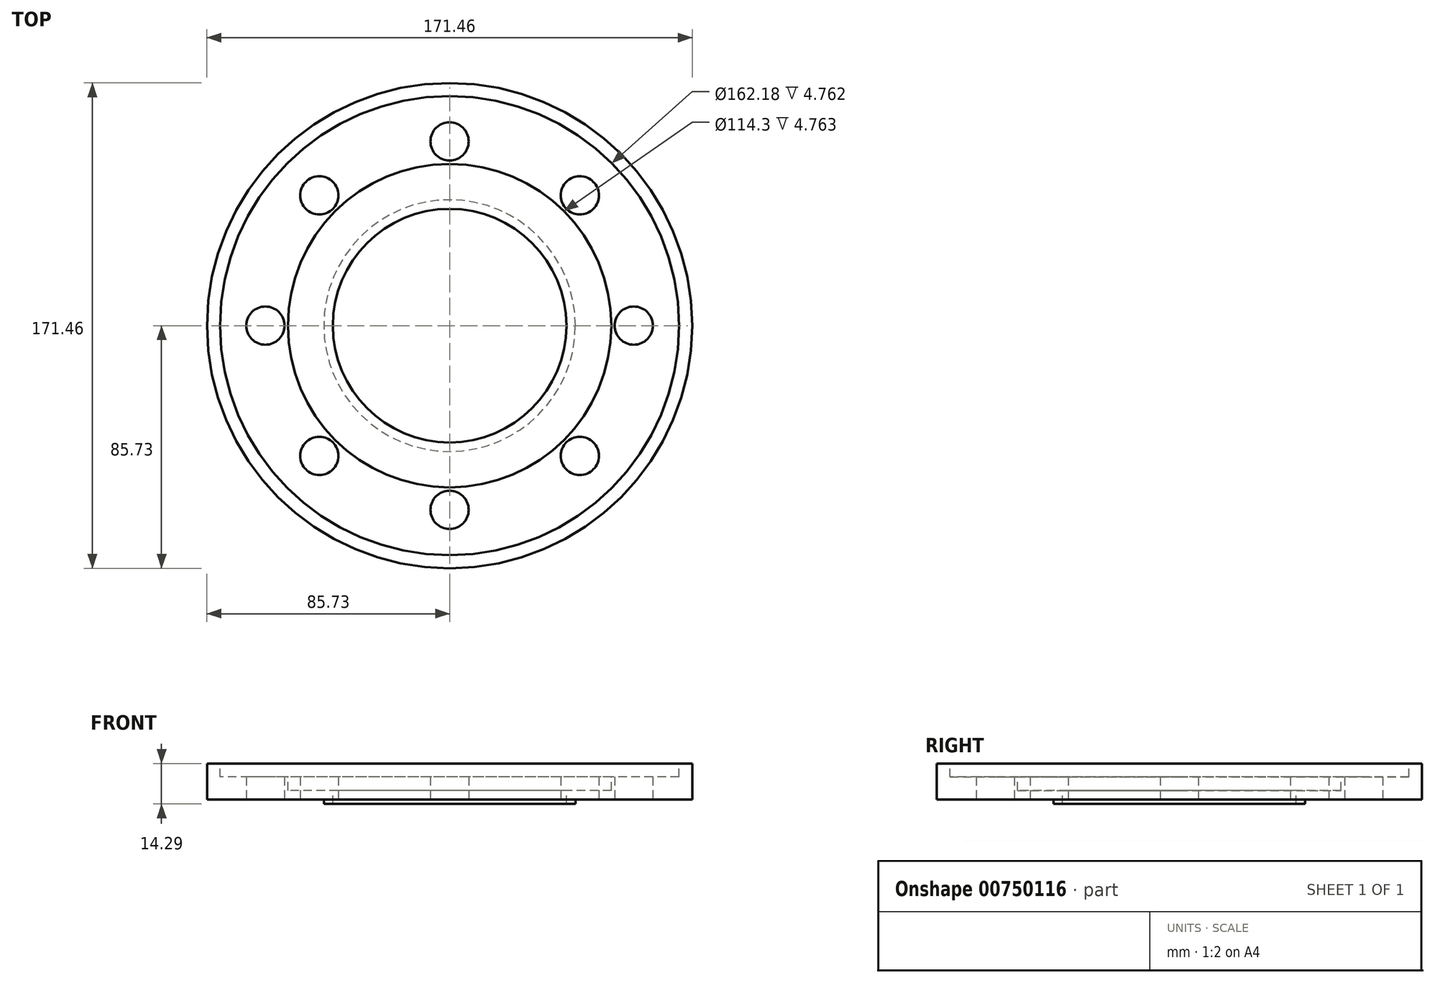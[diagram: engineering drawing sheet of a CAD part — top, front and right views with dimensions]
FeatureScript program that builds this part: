
annotation { "Feature Type Name" : "Feature", "Feature Type Description" : "" }
export const myFeature = defineFeature(function(context is Context, id is Id, definition is map)
    precondition{}
    {
        {
            var Q0;
            Q0=qCreatedBy(makeId("Front.planeOp"),FACE);
            var sketch = newSketch(context, id + "F0", { "sketchPlane" : qUnion([Q0])});
            skLineSegment(sketch, "E0", {"start": v(44.45, 0) * mm, "end": v(44.45, 1.59) * mm});
            skLineSegment(sketch, "E1", {"start": v(44.45, 1.59) * mm, "end": v(85.73, 1.59) * mm});
            skLineSegment(sketch, "E2", {"start": v(85.73, 1.59) * mm, "end": v(85.73, 9.53) * mm});
            skLineSegment(sketch, "E3", {"start": v(57.15, 9.53) * mm, "end": v(57.15, 9.53) * mm});
            skLineSegment(sketch, "E4", {"start": v(41.28, 0) * mm, "end": v(44.45, 0) * mm});
            skLineSegment(sketch, "E5", {"start": v(85.73, 9.53) * mm, "end": v(85.73, 14.29) * mm});
            skLineSegment(sketch, "E6", {"start": v(85.73, 14.29) * mm, "end": v(81.09, 14.29) * mm});
            skLineSegment(sketch, "E7", {"start": v(0, 22.95) * mm, "end": v(0, 0) * mm, "construction": true});
            skLineSegment(sketch, "E8", {"start": v(41.28, 0) * mm, "end": v(41.28, 4.76) * mm});
            skLineSegment(sketch, "E9", {"start": v(41.28, 4.76) * mm, "end": v(57.15, 4.76) * mm});
            skLineSegment(sketch, "E10", {"start": v(57.15, 4.76) * mm, "end": v(57.15, 9.53) * mm});
            skLineSegment(sketch, "E11", {"start": v(57.15, 9.53) * mm, "end": v(81.09, 9.53) * mm});
            skLineSegment(sketch, "E12", {"start": v(81.09, 14.29) * mm, "end": v(81.09, 9.53) * mm});
            skSolve(sketch);
        }
        {
            var Q0;
            Q0=makeQuery(id+"F0.imprint","IMPRINT",FACE,{"disambiguationData":[TD([[makeQuery(id+"F0.imprint","IMPRINT",EDGE,{"derivedFrom":sQuery(id+"F0.wireOp",EDGE,"E0")}),1.0]])]});
            var Q1;
            Q1=sQuery(id+"F0.wireOp",EDGE,"E7");
            revolve(context, id + "F1", {"surfaceOperationType" : NewSurfaceOperationType.NEW, "entities" : qUnion([Q0]), "axis" : qUnion([Q1]), "revolveType" : RevolveType.FULL});
        }
        {
            var Q0;
            Q0=makeQuery(id+"F1.opRevolve","SWEPT_FACE",FACE,{"disambiguationData":[OSD([sQuery(id+"F0.wireOp",EDGE,"E1")])]});
            var sketch = newSketch(context, id + "F2", { "sketchPlane" : qUnion([Q0])});
            skCircle(sketch, "E13", {"center": v(0, 0) * mm, "radius": 65.09 * mm});
            skPoint(sketch, "E14", {"position": v(0, 65.09) * mm});
            skPoint(sketch, "E15.1.0", {"position": v(-46.02, 46.02) * mm});
            skPoint(sketch, "E15.2.0", {"position": v(-65.09, 0) * mm});
            skPoint(sketch, "E15.3.0", {"position": v(-46.02, -46.02) * mm});
            skPoint(sketch, "E15.4.0", {"position": v(0, -65.09) * mm});
            skPoint(sketch, "E15.5.0", {"position": v(46.02, -46.02) * mm});
            skPoint(sketch, "E15.6.0", {"position": v(65.09, 0) * mm});
            skPoint(sketch, "E15.7.0", {"position": v(46.02, 46.02) * mm});
            skSolve(sketch);
        }
        {
            var Q0;
            Q0=sQuery(id+"F2.wireOp",VERTEX,"E14");
            var Q1;
            Q1=sQuery(id+"F2.wireOp",VERTEX,"E15.1.0");
            var Q2;
            Q2=sQuery(id+"F2.wireOp",VERTEX,"E15.2.0");
            var Q3;
            Q3=sQuery(id+"F2.wireOp",VERTEX,"E15.3.0");
            var Q4;
            Q4=sQuery(id+"F2.wireOp",VERTEX,"E15.4.0");
            var Q5;
            Q5=sQuery(id+"F2.wireOp",VERTEX,"E15.5.0");
            var Q6;
            Q6=sQuery(id+"F2.wireOp",VERTEX,"E15.6.0");
            var Q7;
            Q7=sQuery(id+"F2.wireOp",VERTEX,"E15.7.0");
            var Q8;
            Q8=makeQuery(id+"F1.opRevolve","SWEPT_BODY",BODY,{"disambiguationData":[OSD([sQuery(id+"F0.wireOp",EDGE,"E0"),sQuery(id+"F0.wireOp",EDGE,"E1"),sQuery(id+"F0.wireOp",EDGE,"E2"),sQuery(id+"F0.wireOp",EDGE,"E4"),sQuery(id+"F0.wireOp",EDGE,"E5"),sQuery(id+"F0.wireOp",EDGE,"E6"),sQuery(id+"F0.wireOp",EDGE,"E8"),sQuery(id+"F0.wireOp",EDGE,"E9"),sQuery(id+"F0.wireOp",EDGE,"E10"),sQuery(id+"F0.wireOp",EDGE,"E11"),sQuery(id+"F0.wireOp",EDGE,"E12")])]});
            hole(context, id + "F3", {"style" : HoleStyle.SIMPLE, "endStyle" : HoleEndStyle.THROUGH, "standardTappedOrClearance" : lookupTablePath({ "fit" : "Normal (ASME)", "standard" : "ANSI", "size" : "1/2", "type" : "Clearance" }), "standardBlindInLast" : lookupTablePath({ "fit" : "Free", "standard" : "ANSI", "size" : "1/2", "type" : "Clearance" }), "holeDiameter" : 13.5 * mm, "majorDiameter" : 6.35 * mm, "isTappedThrough" : true, "tappedDepth" : 12.7 * mm, "tapClearance" : 3, "locations" : qUnion([Q0, Q1, Q2, Q3, Q4, Q5, Q6, Q7]), "scope" : qUnion([Q8])});
        }
    });
